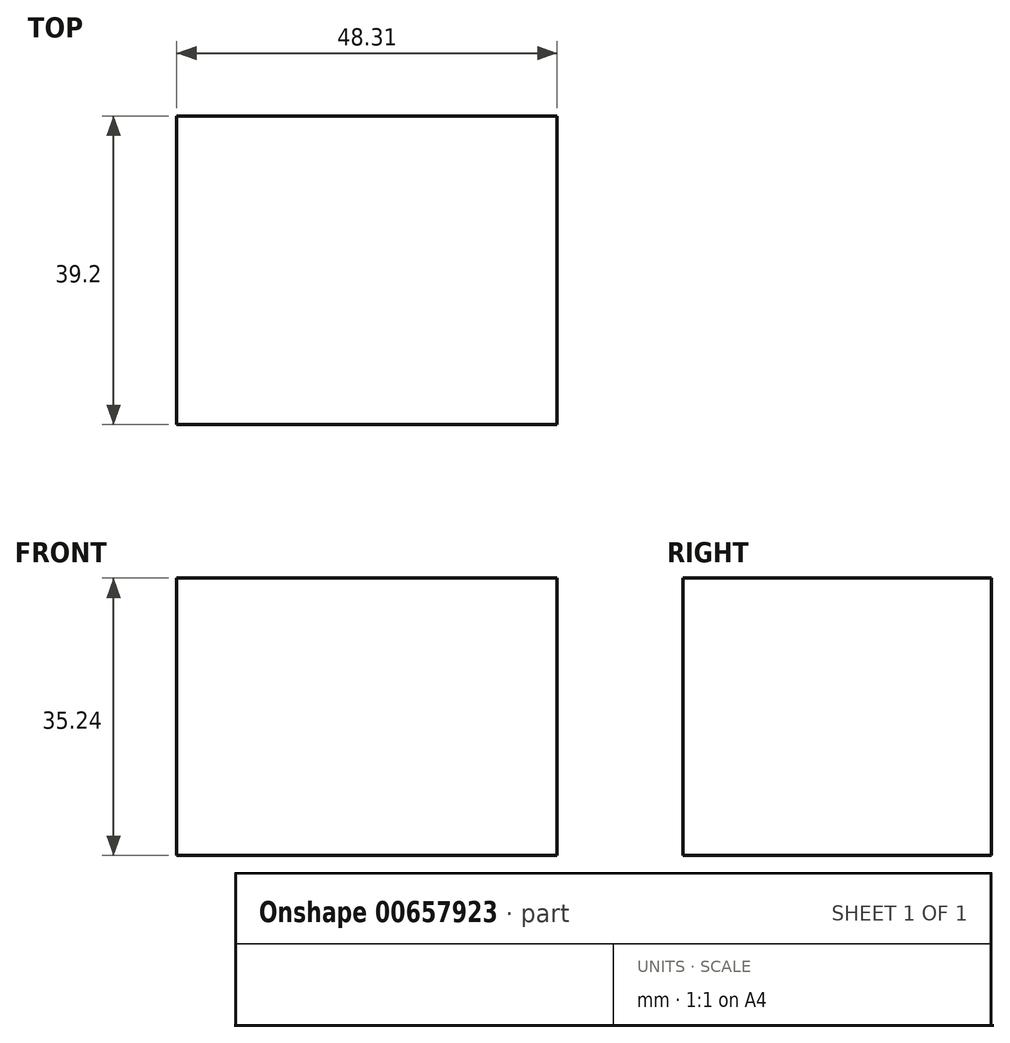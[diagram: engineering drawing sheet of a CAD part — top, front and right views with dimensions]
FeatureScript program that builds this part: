
annotation { "Feature Type Name" : "Feature", "Feature Type Description" : "" }
export const myFeature = defineFeature(function(context is Context, id is Id, definition is map)
    precondition{}
    {
        {
            var Q0;
            Q0=qCreatedBy(makeId("Front.planeOp"),FACE);
            var sketch = newSketch(context, id + "F0", { "sketchPlane" : qUnion([Q0])});
            skLineSegment(sketch, "E0.bottom", {"start": v(-48.3, 19.01) * mm, "end": v(0, 19.01) * mm});
            skLineSegment(sketch, "E0.top", {"start": v(-48.3, -16.23) * mm, "end": v(0, -16.23) * mm});
            skLineSegment(sketch, "E0.left", {"start": v(-48.3, 19.01) * mm, "end": v(-48.3, -16.23) * mm});
            skLineSegment(sketch, "E0.right", {"start": v(0, 19.01) * mm, "end": v(0, -16.23) * mm});
            skSolve(sketch);
        }
        {
            var Q0;
            Q0 = qSketchRegion(id + "F0", true);
            extrude(context, id + "F1", {"entities" : qUnion([Q0]), "depth" : 39.2 * mm, "offsetDistance" : 25 * mm});
        }
    });
